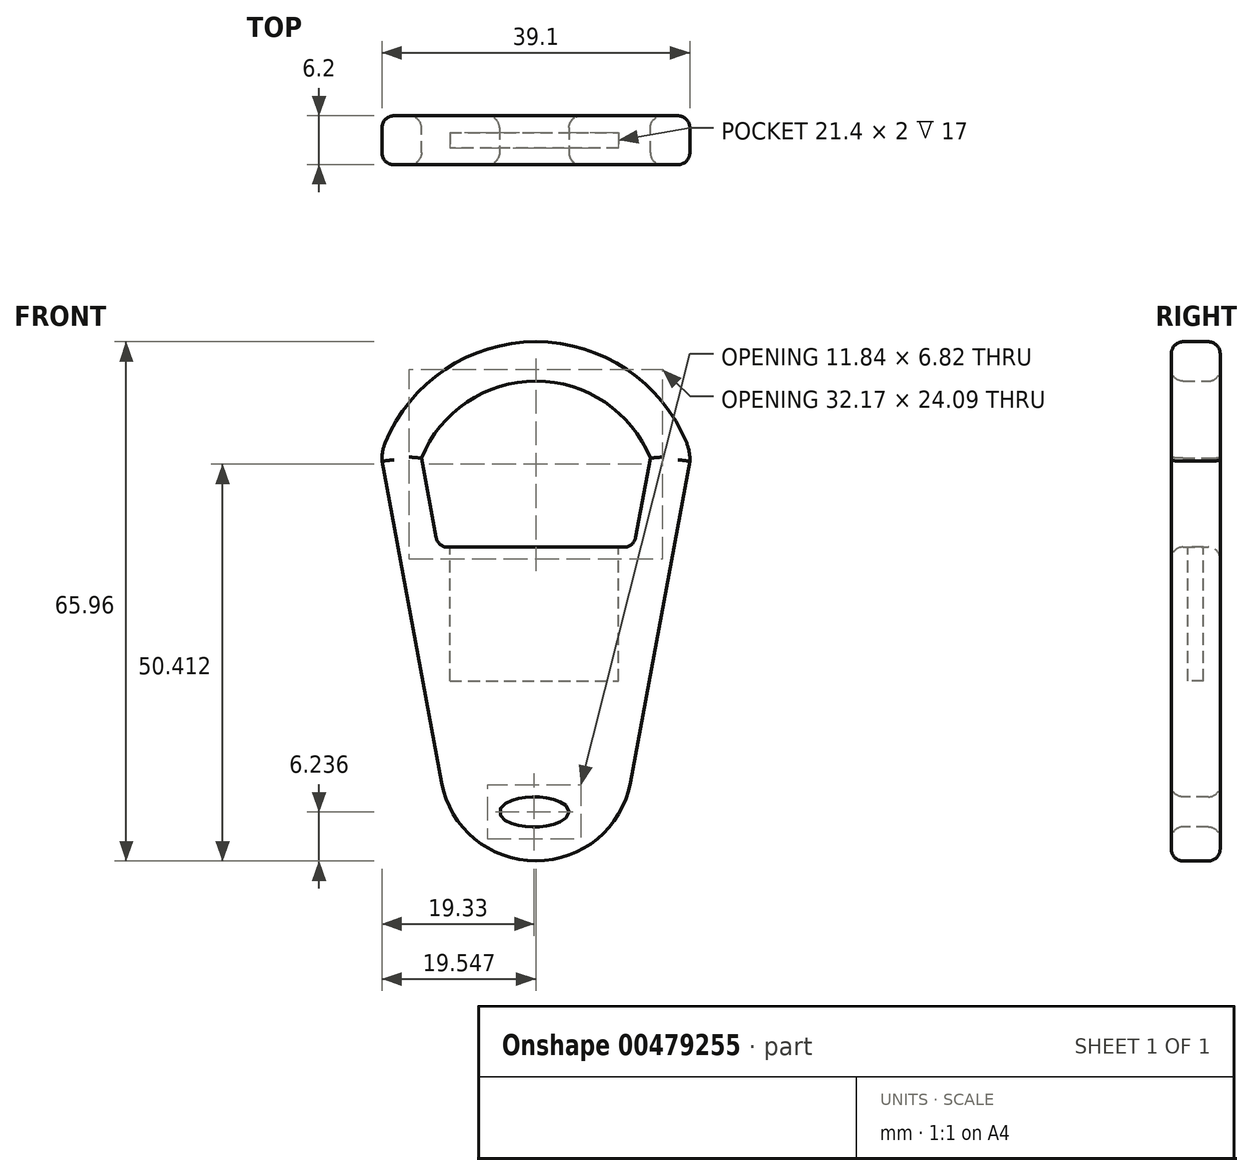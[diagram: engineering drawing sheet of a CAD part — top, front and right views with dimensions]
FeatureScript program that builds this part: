
annotation { "Feature Type Name" : "Feature", "Feature Type Description" : "" }
export const myFeature = defineFeature(function(context is Context, id is Id, definition is map)
    precondition{}
    {
        {
            var Q0;
            Q0=qCreatedBy(makeId("Front.planeOp"),FACE);
            var sketch = newSketch(context, id + "F0", { "sketchPlane" : qUnion([Q0])});
            skLineSegment(sketch, "E0", {"start": v(0.22, 53.5) * mm, "end": v(0.22, -27.22) * mm, "construction": true});
            skLineSegment(sketch, "E1", {"start": v(19.76, 12.33) * mm, "end": v(12.22, -28.48) * mm});
            skLineSegment(sketch, "E2.MirrorCS", {"start": v(-19.33, 12.33) * mm, "end": v(-11.78, -28.48) * mm});
            skLineSegment(sketch, "E3.0", {"start": v(-14.31, 12.71) * mm, "end": v(-12.22, 1.4) * mm});
            skLineSegment(sketch, "E3.3", {"start": v(14.75, 12.71) * mm, "end": v(12.66, 1.4) * mm});
            skLineSegment(sketch, "E4", {"start": v(-12.22, 1.4) * mm, "end": v(12.66, 1.4) * mm});
            skPoint(sketch, "E5", {"position": v(0.22, 20.6) * mm});
            skPoint(sketch, "E6", {"position": v(-14.31, 12.71) * mm});
            skPoint(sketch, "E7.MirrorP", {"position": v(14.75, 12.71) * mm});
            skArc(sketch, "E8", {"start": v(14.75, 12.71) * mm, "mid": v(0.22, 22.5) * mm, "end": v(-14.31, 12.71) * mm});
            skArc(sketch, "E9.0", {"start": v(19.62, 13.97) * mm, "mid": v(0.56, 27.5) * mm, "end": v(-18.94, 14.6) * mm});
            skArc(sketch, "E10", {"start": v(-18.94, 14.6) * mm, "mid": v(-19.26, 13.5) * mm, "end": v(-19.33, 12.33) * mm});
            skArc(sketch, "E11.MirrorCS", {"start": v(19.38, 14.6) * mm, "mid": v(19.7, 13.5) * mm, "end": v(19.76, 12.33) * mm});
            skPoint(sketch, "E12.orphan", {"position": v(-21.9, 26.19) * mm});
            skPoint(sketch, "E13.orphan", {"position": v(22.32, 26.19) * mm});
            skPoint(sketch, "E14.MirrorCS.start.orphan", {"position": v(0.22, 25.6) * mm});
            skArc(sketch, "E15", {"start": v(-11.78, -28.48) * mm, "mid": v(0.22, -38.46) * mm, "end": v(12.22, -28.48) * mm});
            skPoint(sketch, "E16.MirrorCS.end.orphan", {"position": v(0.22, -28.48) * mm});
            skPoint(sketch, "E16.MirrorCS.start.orphan", {"position": v(-11.78, -28.48) * mm});
            skLineSegment(sketch, "E17", {"start": v(-11.78, -28.48) * mm, "end": v(12.22, -28.48) * mm, "construction": true});
            skSolve(sketch);
        }
        {
            var Q0;
            Q0=qSketchRegion(id+"F0",true);
            extrude(context, id + "F1", {"entities" : qUnion([Q0]), "depth" : 6.2 * mm});
        }
        {
            var Q0;
            Q0=makeQuery(id+"F1.opExtrude","CAP_FACE",FACE,{"disambiguationData":[OSD([sQuery(id+"F0.wireOp",EDGE,"E1"),sQuery(id+"F0.wireOp",EDGE,"E2.MirrorCS"),sQuery(id+"F0.wireOp",EDGE,"E3.0"),sQuery(id+"F0.wireOp",EDGE,"E3.3"),sQuery(id+"F0.wireOp",EDGE,"E4"),sQuery(id+"F0.wireOp",EDGE,"E8"),sQuery(id+"F0.wireOp",EDGE,"E9.0"),sQuery(id+"F0.wireOp",EDGE,"E10"),sQuery(id+"F0.wireOp",EDGE,"E11.MirrorCS"),sQuery(id+"F0.wireOp",EDGE,"E15")])],"isStart":false});
            var sketch = newSketch(context, id + "F2", { "sketchPlane" : qUnion([Q0])});
            skEllipse(sketch, "E18", {"center": v(0, -32.22) * mm, "majorRadius": 4.42 * mm, "minorRadius": 1.9 * mm, "majorAxis": v(1, 0)});
            skSolve(sketch);
        }
        {
            var Q0;
            Q0=makeQuery(id+"F2.imprint","IMPRINT",FACE,{"disambiguationData":[TD([[makeQuery(id+"F2.imprint","IMPRINT",EDGE,{"derivedFrom":sQuery(id+"F2.wireOp",EDGE,"E18")}),1.0]])]});
            extrude(context, id + "F3", {"entities" : qUnion([Q0]), "operationType" : NewBodyOperationType.REMOVE, "oppositeDirection" : true, "depth" : 6.5 * mm});
        }
        {
            var Q0;
            Q0=makeQuery(id+"F1.opExtrude","SWEPT_FACE",FACE,{"disambiguationData":[OSD([sQuery(id+"F0.wireOp",EDGE,"E4")])]});
            var sketch = newSketch(context, id + "F4", { "sketchPlane" : qUnion([Q0])});
            skLineSegment(sketch, "E19", {"start": v(0, -2.1) * mm, "end": v(10.7, -2.1) * mm});
            skLineSegment(sketch, "E20.0", {"start": v(0, -4.1) * mm, "end": v(10.7, -4.1) * mm});
            skLineSegment(sketch, "E21", {"start": v(10.7, -2.1) * mm, "end": v(10.7, -4.1) * mm});
            skLineSegment(sketch, "E22", {"start": v(0, -2.1) * mm, "end": v(0, -4.1) * mm, "construction": true});
            skLineSegment(sketch, "E23.MirrorCS", {"start": v(0, -2.1) * mm, "end": v(-10.7, -2.1) * mm});
            skLineSegment(sketch, "E24.MirrorCS", {"start": v(-10.7, -2.1) * mm, "end": v(-10.7, -4.1) * mm});
            skLineSegment(sketch, "E25.MirrorCS", {"start": v(0, -4.1) * mm, "end": v(-10.7, -4.1) * mm});
            skSolve(sketch);
        }
        {
            var Q0;
            Q0=makeQuery(id+"F4.imprint","IMPRINT",FACE,{"disambiguationData":[TD([[makeQuery(id+"F4.imprint","IMPRINT",EDGE,{"derivedFrom":sQuery(id+"F4.wireOp",EDGE,"E19")}),-1.0]])]});
            extrude(context, id + "F5", {"entities" : qUnion([Q0]), "operationType" : NewBodyOperationType.REMOVE, "oppositeDirection" : true, "depth" : 17 * mm});
        }
        {
            var Q0;
            Q0=makeQuery(id+"F1.opExtrude","SWEPT_EDGE",EDGE,{"disambiguationData":[OSD([sQuery(id+"F0.wireOp",EDGE,"E3.0"),sQuery(id+"F0.wireOp",EDGE,"E4")])]});
            var Q1;
            Q1=makeQuery(id+"F1.opExtrude","SWEPT_EDGE",EDGE,{"disambiguationData":[OSD([sQuery(id+"F0.wireOp",EDGE,"E3.3"),sQuery(id+"F0.wireOp",EDGE,"E4")])]});
            var Q2;
            Q2=makeQuery(id+"F1.opExtrude","CAP_FACE",FACE,{"disambiguationData":[OSD([sQuery(id+"F0.wireOp",EDGE,"E1"),sQuery(id+"F0.wireOp",EDGE,"E2.MirrorCS"),sQuery(id+"F0.wireOp",EDGE,"E3.0"),sQuery(id+"F0.wireOp",EDGE,"E3.3"),sQuery(id+"F0.wireOp",EDGE,"E4"),sQuery(id+"F0.wireOp",EDGE,"E8"),sQuery(id+"F0.wireOp",EDGE,"E9.0"),sQuery(id+"F0.wireOp",EDGE,"E10"),sQuery(id+"F0.wireOp",EDGE,"E11.MirrorCS"),sQuery(id+"F0.wireOp",EDGE,"E15")])],"isStart":false});
            var Q3;
            Q3=makeQuery(id+"F1.opExtrude","CAP_FACE",FACE,{"disambiguationData":[OSD([sQuery(id+"F0.wireOp",EDGE,"E1"),sQuery(id+"F0.wireOp",EDGE,"E2.MirrorCS"),sQuery(id+"F0.wireOp",EDGE,"E3.0"),sQuery(id+"F0.wireOp",EDGE,"E3.3"),sQuery(id+"F0.wireOp",EDGE,"E4"),sQuery(id+"F0.wireOp",EDGE,"E8"),sQuery(id+"F0.wireOp",EDGE,"E9.0"),sQuery(id+"F0.wireOp",EDGE,"E10"),sQuery(id+"F0.wireOp",EDGE,"E11.MirrorCS"),sQuery(id+"F0.wireOp",EDGE,"E15")])],"isStart":true});
            fillet(context, id + "F6", {"entities" : qUnion([Q0, Q1, Q2, Q3]), "radius" : 1.5 * mm, "tangentPropagation" : true, "allowEdgeOverflow" : false});
        }
    });
